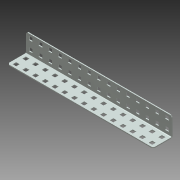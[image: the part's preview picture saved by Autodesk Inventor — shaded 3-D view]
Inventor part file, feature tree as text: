
AUTODESK INVENTOR PART (.ipt)
format: ipt  version: 2013 (Build 170138000, 138)  size: 602,112 bytes
history: native  units: mm (DEFAULTED — no unit token found)
features: other x64, extrude x60, sketch x5, sheet_metal_op x3, pattern_linear x2
ambient origin geometry x8: Origin, YZ Plane, XZ Plane, XY Plane, X Axis, Y Axis, Z Axis, Center Point
bodies: Solid1 (feature_tree)
feature tree (134):
  sheet_metal_op  "Face1"
  sheet_metal_op  "Flange1"
  other  "Corner Chamfer1"
  pattern_linear  "Rectangular Pattern1"  Spacing1=24.13mm  [1 undecoded]
  pattern_linear  "Rectangular Pattern2"  Count1=15 Spacing1=12.7mm
  sketch  "Sketch1"  dims[d0=2.794mm]
  other  "Plate1"
  sketch  "Sketch2"  dims[d1=8.128mm]
  other  "Plate2"
  sheet_metal_op  "Bend1"
  sketch  "Sketch3"  dims[d2=4.572mm]
  sketch  "Sketch4"  dims[d3=4.572mm]
  other  "Srf1"
  other  "Srf2"
  other  "Srf3"
  other  "Srf4"
  other  "Srf5"
  other  "Srf6"
  other  "Srf7"
  other  "Srf8"
  other  "Srf9"
  other  "Srf10"
  other  "Srf11"
  other  "Srf12"
  other  "Srf13"
  other  "Srf14"
  other  "Srf15"
  other  "Srf16"
  other  "Srf17"
  other  "Srf18"
  other  "Srf19"
  other  "Srf20"
  other  "Srf21"
  other  "Srf22"
  other  "Srf23"
  other  "Srf24"
  other  "Srf25"
  other  "Srf26"
  other  "Srf27"
  other  "Srf28"
  other  "Srf29"
  other  "Srf30"
  sketch  "Sketch5"  dims[d4=4.572mm d5=24.13mm d6=150.0mm d8=12.7mm d9=10.0mm d11=25.4mm d13=4.064mm d14=0.8636mm d15=1.27mm d16=0.635mm d17=2.54mm d18=0.8636mm d19=24.13mm d20=90.0deg d21=0.8636mm d22=1.905mm d23=6.35mm d24=45.0deg d25=4.572mm d26=4.572mm d27=8.128mm d28=4.064mm d29=2.794mm d30=4.572mm d31=4.064mm d32=150.0mm d34=12.7mm d35=10.0mm d37=25.4mm d39=1.27mm d40=0.0mm d41=25.4mm d42=0.0mm d43=150.0mm d45=12.7mm d46=20.0mm d48=12.7mm d49=0.0mm d50=0.0mm d51=0.0mm d52=0.0mm d53=0.0mm d54=0.0mm d55=0.0mm d56=0.0mm d57=0.0mm d58=0.0mm d59=0.0mm d60=0.0mm d61=0.0mm d62=0.0mm d63=0.0mm d64=0.0mm d65=0.0mm d66=0.0mm d67=0.0mm d68=0.0mm d69=0.0mm d70=0.0mm d71=0.0mm d72=0.0mm d73=0.0mm d74=0.0mm d75=0.0mm d76=0.0mm d77=0.0mm d78=0.0mm d79=0.0mm d80=0.0mm d81=0.0mm d82=0.0mm d83=0.0mm d84=0.0mm d85=0.0mm d86=0.0mm d87=0.0mm d88=0.0mm d89=0.0mm d90=0.0mm d91=0.0mm d92=0.0mm d93=0.0mm d94=0.0mm d95=0.0mm d96=0.0mm d97=0.0mm d98=0.0mm d99=0.0mm d100=0.0mm d101=0.0mm d102=0.0mm d103=0.0mm d104=0.0mm d105=0.0mm d106=0.0mm d107=0.0mm d108=0.0mm d109=25.4mm d110=0.0mm d111=150.0mm d113=12.7mm d114=20.0mm d116=12.7mm d117=0.0mm d118=0.0mm d119=0.0mm d120=0.0mm d121=0.0mm d122=0.0mm d123=0.0mm d124=0.0mm d125=0.0mm d126=0.0mm d127=0.0mm d128=0.0mm d129=0.0mm d130=0.0mm d131=0.0mm d132=0.0mm d133=0.0mm d134=0.0mm d135=0.0mm d136=0.0mm d137=0.0mm d138=0.0mm d139=0.0mm d140=0.0mm d141=0.0mm d142=0.0mm d143=0.0mm d144=0.0mm d145=0.0mm d146=0.0mm d147=0.0mm d148=0.0mm d149=0.0mm d150=0.0mm d151=0.0mm d152=0.0mm d153=0.0mm d154=0.0mm d155=0.0mm d156=0.0mm d157=0.0mm d158=0.0mm d159=0.0mm d160=0.0mm d161=0.0mm d162=0.0mm d163=0.0mm d164=0.0mm d165=0.0mm d166=0.0mm d167=0.0mm d168=0.0mm d169=0.0mm d170=0.0mm d171=0.0mm d172=0.0mm d173=0.0mm d174=0.0mm d175=0.0mm d176=0.0mm]
  other  "Srf31"
  other  "Srf32"
  other  "Srf33"
  other  "Srf34"
  other  "Srf35"
  other  "Srf36"
  other  "Srf37"
  other  "Srf38"
  other  "Srf39"
  other  "Srf40"
  other  "Srf41"
  other  "Srf42"
  other  "Srf43"
  other  "Srf44"
  other  "Srf45"
  other  "Srf46"
  other  "Srf47"
  other  "Srf48"
  other  "Srf49"
  other  "Srf50"
  other  "Srf51"
  other  "Srf52"
  other  "Srf53"
  other  "Srf54"
  other  "Srf55"
  other  "Srf56"
  other  "Srf57"
  other  "Srf58"
  other  "Srf59"
  other  "Srf60"
  other  "Cut1"
  extrude  "ExtrusionSrf1"  Depth=4.064mm
  extrude  "ExtrusionSrf31"  Depth=0.8636mm
  extrude  "ExtrusionSrf2"  Depth=1.27mm
  extrude  "ExtrusionSrf3"  Depth=0.635mm
  extrude  "ExtrusionSrf4"  Depth=2.54mm
  extrude  "ExtrusionSrf5"  Depth=0.8636mm
  extrude  "ExtrusionSrf6"  Depth=24.13mm TaperAngle=90.0deg
  extrude  "ExtrusionSrf7"  Depth=1.905mm TaperAngle=45.0deg
  extrude  "ExtrusionSrf8"  Depth=4.572mm
  extrude  "ExtrusionSrf9"  Depth=4.572mm
  extrude  "ExtrusionSrf10"  Depth=8.128mm
  extrude  "ExtrusionSrf11"  Depth=4.064mm
  extrude  "ExtrusionSrf12"  Depth=2.794mm
  extrude  "ExtrusionSrf13"  Depth=4.572mm
  extrude  "ExtrusionSrf14"  Depth=4.064mm
  extrude  "ExtrusionSrf15"  Depth=150.0mm
  extrude  "ExtrusionSrf16"  Depth=1.27mm
  extrude  "ExtrusionSrf17"  TaperAngle=0.0deg  [1 undecoded]
  extrude  "ExtrusionSrf18"  Depth=25.4mm TaperAngle=0.0deg
  extrude  "ExtrusionSrf19"  Depth=150.0mm
  extrude  "ExtrusionSrf20"  Depth=20.0mm
  extrude  "ExtrusionSrf21"  TaperAngle=0.0deg  [1 undecoded]
  extrude  "ExtrusionSrf22"  TaperAngle=0.0deg  [1 undecoded]
  extrude  "ExtrusionSrf23"  TaperAngle=0.0deg  [1 undecoded]
  extrude  "ExtrusionSrf24"  TaperAngle=0.0deg  [1 undecoded]
  extrude  "ExtrusionSrf25"  TaperAngle=0.0deg  [1 undecoded]
  extrude  "ExtrusionSrf26"  TaperAngle=0.0deg  [1 undecoded]
  extrude  "ExtrusionSrf27"  TaperAngle=0.0deg  [1 undecoded]
  extrude  "ExtrusionSrf28"  TaperAngle=0.0deg  [1 undecoded]
  extrude  "ExtrusionSrf29"  TaperAngle=0.0deg  [1 undecoded]
  extrude  "ExtrusionSrf30"  TaperAngle=0.0deg  [1 undecoded]
  extrude  "ExtrusionSrf32"  TaperAngle=0.0deg  [1 undecoded]
  extrude  "ExtrusionSrf33"  TaperAngle=0.0deg  [1 undecoded]
  extrude  "ExtrusionSrf34"  TaperAngle=0.0deg  [1 undecoded]
  extrude  "ExtrusionSrf35"  TaperAngle=0.0deg  [1 undecoded]
  extrude  "ExtrusionSrf36"  TaperAngle=0.0deg  [1 undecoded]
  extrude  "ExtrusionSrf37"  TaperAngle=0.0deg  [1 undecoded]
  extrude  "ExtrusionSrf38"  TaperAngle=0.0deg  [1 undecoded]
  extrude  "ExtrusionSrf39"  TaperAngle=0.0deg  [1 undecoded]
  extrude  "ExtrusionSrf40"  TaperAngle=0.0deg  [1 undecoded]
  extrude  "ExtrusionSrf41"  TaperAngle=0.0deg  [1 undecoded]
  extrude  "ExtrusionSrf42"  TaperAngle=0.0deg  [1 undecoded]
  extrude  "ExtrusionSrf43"  TaperAngle=0.0deg  [1 undecoded]
  extrude  "ExtrusionSrf44"  TaperAngle=0.0deg  [1 undecoded]
  extrude  "ExtrusionSrf45"  TaperAngle=0.0deg  [1 undecoded]
  extrude  "ExtrusionSrf46"  TaperAngle=0.0deg  [1 undecoded]
  extrude  "ExtrusionSrf47"  TaperAngle=0.0deg  [1 undecoded]
  extrude  "ExtrusionSrf48"  TaperAngle=0.0deg  [1 undecoded]
  extrude  "ExtrusionSrf49"  TaperAngle=0.0deg  [1 undecoded]
  extrude  "ExtrusionSrf50"  TaperAngle=0.0deg  [1 undecoded]
  extrude  "ExtrusionSrf51"  TaperAngle=0.0deg  [1 undecoded]
  extrude  "ExtrusionSrf52"  TaperAngle=0.0deg  [1 undecoded]
  extrude  "ExtrusionSrf53"  TaperAngle=0.0deg  [1 undecoded]
  extrude  "ExtrusionSrf54"  TaperAngle=0.0deg  [1 undecoded]
  extrude  "ExtrusionSrf55"  TaperAngle=0.0deg  [1 undecoded]
  extrude  "ExtrusionSrf56"  TaperAngle=0.0deg  [1 undecoded]
  extrude  "ExtrusionSrf57"  TaperAngle=0.0deg  [1 undecoded]
  extrude  "ExtrusionSrf58"  TaperAngle=0.0deg  [1 undecoded]
  extrude  "ExtrusionSrf59"  TaperAngle=0.0deg  [1 undecoded]
  extrude  "ExtrusionSrf60"  TaperAngle=0.0deg  [1 undecoded]
note: 41 required parameter values undecoded (feature->parameter linkage not recoverable at this tier; creation-order binding heuristic only, values carry confidence <= 0.55)
